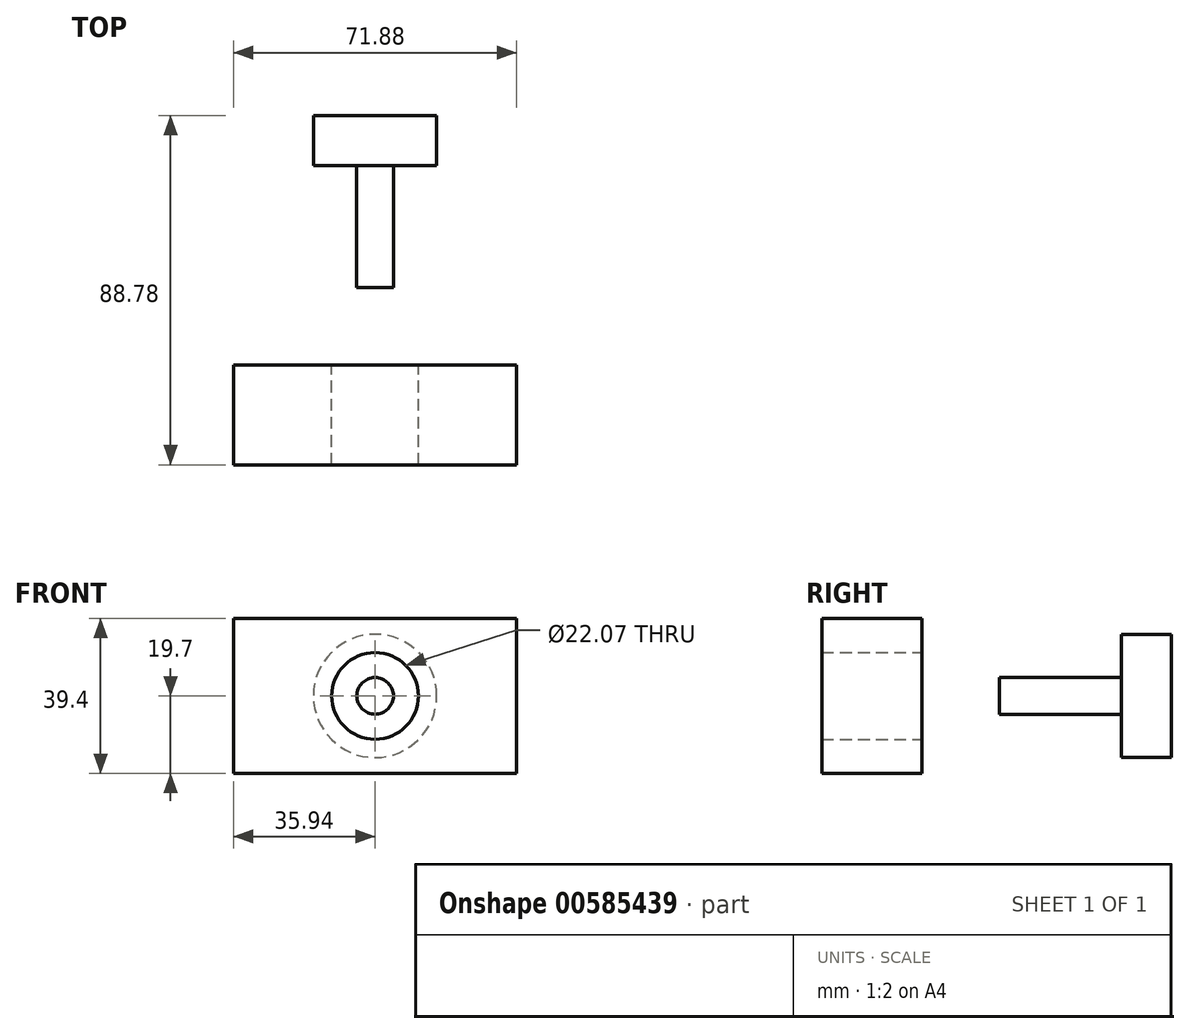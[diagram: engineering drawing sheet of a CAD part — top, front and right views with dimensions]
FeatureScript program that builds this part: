
annotation { "Feature Type Name" : "Feature", "Feature Type Description" : "" }
export const myFeature = defineFeature(function(context is Context, id is Id, definition is map)
    precondition{}
    {
        {
            var Q0;
            Q0=qCreatedBy(makeId("Front.planeOp"),FACE);
            var sketch = newSketch(context, id + "F0", { "sketchPlane" : qUnion([Q0])});
            skLineSegment(sketch, "E0.bottom", {"start": v(-35.94, 19.7) * mm, "end": v(35.94, 19.7) * mm});
            skLineSegment(sketch, "E0.top", {"start": v(-35.94, -19.7) * mm, "end": v(35.94, -19.7) * mm});
            skLineSegment(sketch, "E0.left", {"start": v(-35.94, 19.7) * mm, "end": v(-35.94, -19.7) * mm});
            skLineSegment(sketch, "E0.right", {"start": v(35.94, 19.7) * mm, "end": v(35.94, -19.7) * mm});
            skPoint(sketch, "E0.middle", {"position": v(0, 0) * mm});
            skCircle(sketch, "E1", {"center": v(0, 0) * mm, "radius": 11.04 * mm});
            skSolve(sketch);
        }
        {
            var Q0;
            Q0=makeQuery(id+"F0.imprint","IMPRINT",FACE,{"disambiguationData":[TD([[makeQuery(id+"F0.imprint","IMPRINT",EDGE,{"derivedFrom":sQuery(id+"F0.wireOp",EDGE,"E0.bottom")}),-1.0]])]});
            extrude(context, id + "F1", {"entities" : qUnion([Q0]), "depth" : 25.4 * mm, "offsetDistance" : 25.4 * mm});
        }
        {
            var Q0;
            Q0=qCreatedBy(makeId("Top.planeOp"),FACE);
            var sketch = newSketch(context, id + "F2", { "sketchPlane" : qUnion([Q0])});
            skLineSegment(sketch, "E2.bottom", {"start": v(0, 50.68) * mm, "end": v(-4.66, 50.68) * mm});
            skLineSegment(sketch, "E2.top", {"start": v(0, 19.7) * mm, "end": v(-4.66, 19.7) * mm});
            skLineSegment(sketch, "E2.left", {"start": v(0, 50.68) * mm, "end": v(0, 19.7) * mm});
            skLineSegment(sketch, "E2.right", {"start": v(-4.66, 50.68) * mm, "end": v(-4.66, 19.7) * mm});
            skSolve(sketch);
        }
        {
            var Q0;
            Q0=makeQuery(id+"F2.imprint","IMPRINT",FACE,{"disambiguationData":[TD([[makeQuery(id+"F2.imprint","IMPRINT",EDGE,{"derivedFrom":sQuery(id+"F2.wireOp",EDGE,"E2.bottom")}),1.0]])]});
            var Q1;
            Q1=sQuery(id+"F2.wireOp",EDGE,"E2.left");
            revolve(context, id + "F3", {"entities" : qUnion([Q0]), "axis" : qUnion([Q1]), "revolveType" : RevolveType.FULL});
        }
        {
            var Q0;
            Q0=makeQuery(id+"F3.opRevolve","SWEPT_FACE",FACE,{"disambiguationData":[OSD([sQuery(id+"F2.wireOp",EDGE,"E2.bottom")])]});
            var sketch = newSketch(context, id + "F4", { "sketchPlane" : qUnion([Q0])});
            skCircle(sketch, "E3", {"center": v(0, 0) * mm, "radius": 15.65 * mm});
            skSolve(sketch);
        }
        {
            var Q0;
            Q0 = qSketchRegion(id + "F4", true);
            extrude(context, id + "F5", {"entities" : qUnion([Q0]), "operationType" : NewBodyOperationType.ADD, "depth" : 12.7 * mm, "offsetDistance" : 25.4 * mm});
        }
    });
